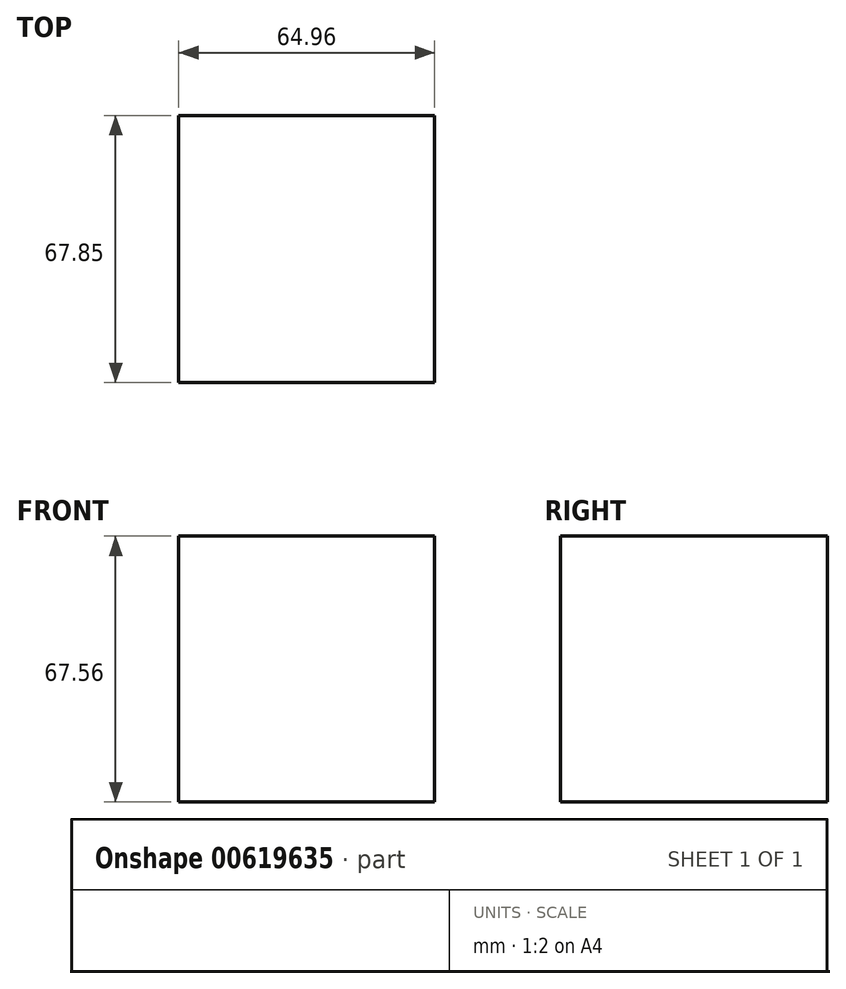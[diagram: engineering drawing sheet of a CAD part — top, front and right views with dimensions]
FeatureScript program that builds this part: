
annotation { "Feature Type Name" : "Feature", "Feature Type Description" : "" }
export const myFeature = defineFeature(function(context is Context, id is Id, definition is map)
    precondition{}
    {
        {
            var Q0;
            Q0=qCreatedBy(makeId("Top.planeOp"),FACE);
            var sketch = newSketch(context, id + "F0", { "sketchPlane" : qUnion([Q0])});
            skLineSegment(sketch, "E0.bottom", {"start": v(0, 0) * mm, "end": v(-64.96, 0) * mm});
            skLineSegment(sketch, "E0.top", {"start": v(0, 67.85) * mm, "end": v(-64.96, 67.85) * mm});
            skLineSegment(sketch, "E0.left", {"start": v(0, 0) * mm, "end": v(0, 67.85) * mm});
            skLineSegment(sketch, "E0.right", {"start": v(-64.96, 0) * mm, "end": v(-64.96, 67.85) * mm});
            skLineSegment(sketch, "E1.bottom", {"start": v(-12.08, 20.29) * mm, "end": v(-21.8, 20.29) * mm});
            skLineSegment(sketch, "E1.top", {"start": v(-12.08, 34.57) * mm, "end": v(-21.8, 34.57) * mm});
            skLineSegment(sketch, "E1.left", {"start": v(-12.08, 20.29) * mm, "end": v(-12.08, 34.57) * mm});
            skLineSegment(sketch, "E1.right", {"start": v(-21.8, 20.29) * mm, "end": v(-21.8, 34.57) * mm});
            skSolve(sketch);
        }
        {
            var Q0;
            Q0=makeQuery(id+"F0.imprint","IMPRINT",FACE,{"disambiguationData":[TD([[makeQuery(id+"F0.imprint","IMPRINT",EDGE,{"derivedFrom":sQuery(id+"F0.wireOp",EDGE,"E0.bottom")}),-1.0]])]});
            var Q1;
            Q1=makeQuery(id+"F0.imprint","IMPRINT",FACE,{"disambiguationData":[TD([[makeQuery(id+"F0.imprint","IMPRINT",EDGE,{"derivedFrom":sQuery(id+"F0.wireOp",EDGE,"E1.bottom")}),-1.0]])]});
            extrude(context, id + "F1", {"entities" : qUnion([Q0, Q1]), "depth" : 67.56 * mm, "offsetDistance" : 25.4 * mm});
        }
    });
